# Revit family: Diffuser-Carnes-SETA-T_Bar
name_source: partatom
category: Duct Accessories
revit_build: Autodesk Revit Architecture 2012 (Build: 20110309_2315(x64)
units: mm (PartAtom-declared; Revit-internal decimal feet)

## types (34) — shared parameters
Catalog = http://www.carnes.com
Default Elevation = 0"
Description = Square and Rectangular Diffusers
Flow = 0 CFM
Manufacturer = CARNES COMPANY
Model = SETA
Product Page URL = http://www.carnes.com
Rapid Induction Vanes = http://www.carnes.com
Round Neck Option = http://www.carnes.com
Specification Sheet = http://www.carnes.com
Subcatagory = Air Distribution
URL = http://www.carnes.com
Unit = Metal - Carnes - Aluminum Polished

## per-type parameters (varying)
| type | Blade Offset | Diffuser Depth B | Diffuser Width A | Duct Height | Duct Width | Plate Depth D | Plate Width C |
| SETA 6x6 11 | 3/4" | 6" | 6" | 6" | 6" | 11 3/4" | 11 3/4" |
| SETA 6x6 47 | 3/4" | 6" | 6" | 6" | 6" | 47 3/4" | 47 3/4" |
| SETA 6x9 11 | 3/4" | 9" | 6" | 9" | 6" | 11 3/4" | 11 3/4" |
| SETA 6x9 47 | 3/4" | 9" | 6" | 9" | 6" | 47 3/4" | 47 3/4" |
| SETA 6x12 11 | 3/4" | 12" | 6" | 12" | 6" | 23 3/4" | 11 3/4" |
| SETA 6x12 47 | 3/4" | 12" | 6" | 12" | 6" | 47 3/4" | 47 3/4" |
| SETA 6x15 11 | 3/4" | 15" | 6" | 15" | 6" | 23 3/4" | 11 3/4" |
| SETA 6x15 47 | 3/4" | 15" | 6" | 15" | 6" | 47 3/4" | 47 3/4" |
| SETA 6x18 11 | 3/4" | 18" | 6" | 18" | 6" | 23 3/4" | 11 3/4" |
| SETA 6x18  47 | 3/4" | 18" | 6" | 18" | 6" | 47 3/4" | 47 3/4" |
| SETA 6x21 11 | 3/4" | 21" | 6" | 21" | 6" | 23 3/4" | 11 3/4" |
| SETA 6x21 47 | 3/4" | 21" | 6" | 21" | 6" | 47 3/4" | 47 3/4" |
| SETA 9x9 11 | 1 1/2" | 9" | 9" | 9" | 9" | 11 3/4" | 11 3/4" |
| SETA 9x9 47 | 1 1/2" | 9" | 9" | 9" | 9" | 47 3/4" | 47 3/4" |
| SETA 9x12 11 | 1 1/2" | 12" | 9" | 12" | 9" | 23 3/4" | 11 3/4" |
| SETA 9x12 47 | 1 1/2" | 12" | 9" | 12" | 9" | 47 3/4" | 47 3/4" |
| SETA 9x15 11 | 1 1/2" | 15" | 9" | 15" | 9" | 23 3/4" | 11 3/4" |
| SETA 9x15 47 | 1 1/2" | 15" | 9" | 15" | 9" | 47 3/4" | 47 3/4" |
| SETA 9x18 11 | 1 1/2" | 18" | 9" | 18" | 9" | 23 3/4" | 11 3/4" |
| SETA 9x18 47 | 1 1/2" | 18" | 9" | 18" | 9" | 47 3/4" | 47 3/4" |
| SETA 9x21 11 | 1 1/2" | 21" | 9" | 21" | 9" | 47 3/4" | 47 3/4" |
| SETA 9x21 47 | 1 1/2" | 21" | 9" | 21" | 9" | 47 3/4" | 47 3/4" |
| SETA 12x12 47 | 1 1/2" | 12" | 12" | 12" | 12" | 47 3/4" | 47 3/4" |
| SETA 12x15 47 | 1 1/2" | 15" | 12" | 15" | 12" | 47 3/4" | 47 3/4" |
| SETA 12x18 47 | 1 1/2" | 18" | 12" | 18" | 12" | 47 3/4" | 47 3/4" |
| SETA 12x21 47 | 1 1/2" | 21" | 12" | 21" | 12" | 47 3/4" | 47 3/4" |
| SETA 15x15 47 | 1 1/2" | 15" | 15" | 15" | 15" | 47 3/4" | 47 3/4" |
| SETA 15x18 47 | 1 1/2" | 18" | 15" | 18" | 15" | 47 3/4" | 47 3/4" |
| SETA 15x21 47 | 1 1/2" | 21" | 15" | 21" | 15" | 47 3/4" | 47 3/4" |
| SETA 18x18 47 | 1 1/2" | 18" | 18" | 18" | 18" | 47 3/4" | 47 3/4" |
| SETA 18x21 47 | 1 1/2" | 21" | 18" | 21" | 18" | 47 3/4" | 47 3/4" |
| SETA 21x21 47 | 1 1/2" | 21" | 21" | 21" | 21" | 47 3/4" | 47 3/4" |
| SETA 21x24 47 | 1 1/2" | 24" | 21" | 24" | 21" | 47 3/4" | 47 3/4" |
| SETA 24x24 47 | 1 1/2" | 24" | 24" | 24" | 24" | 47 3/4" | 47 3/4" |

## geometry (parser evidence)
native form markers: Blend x4, Sweep x2
no freeform markers — native parametric forms only
